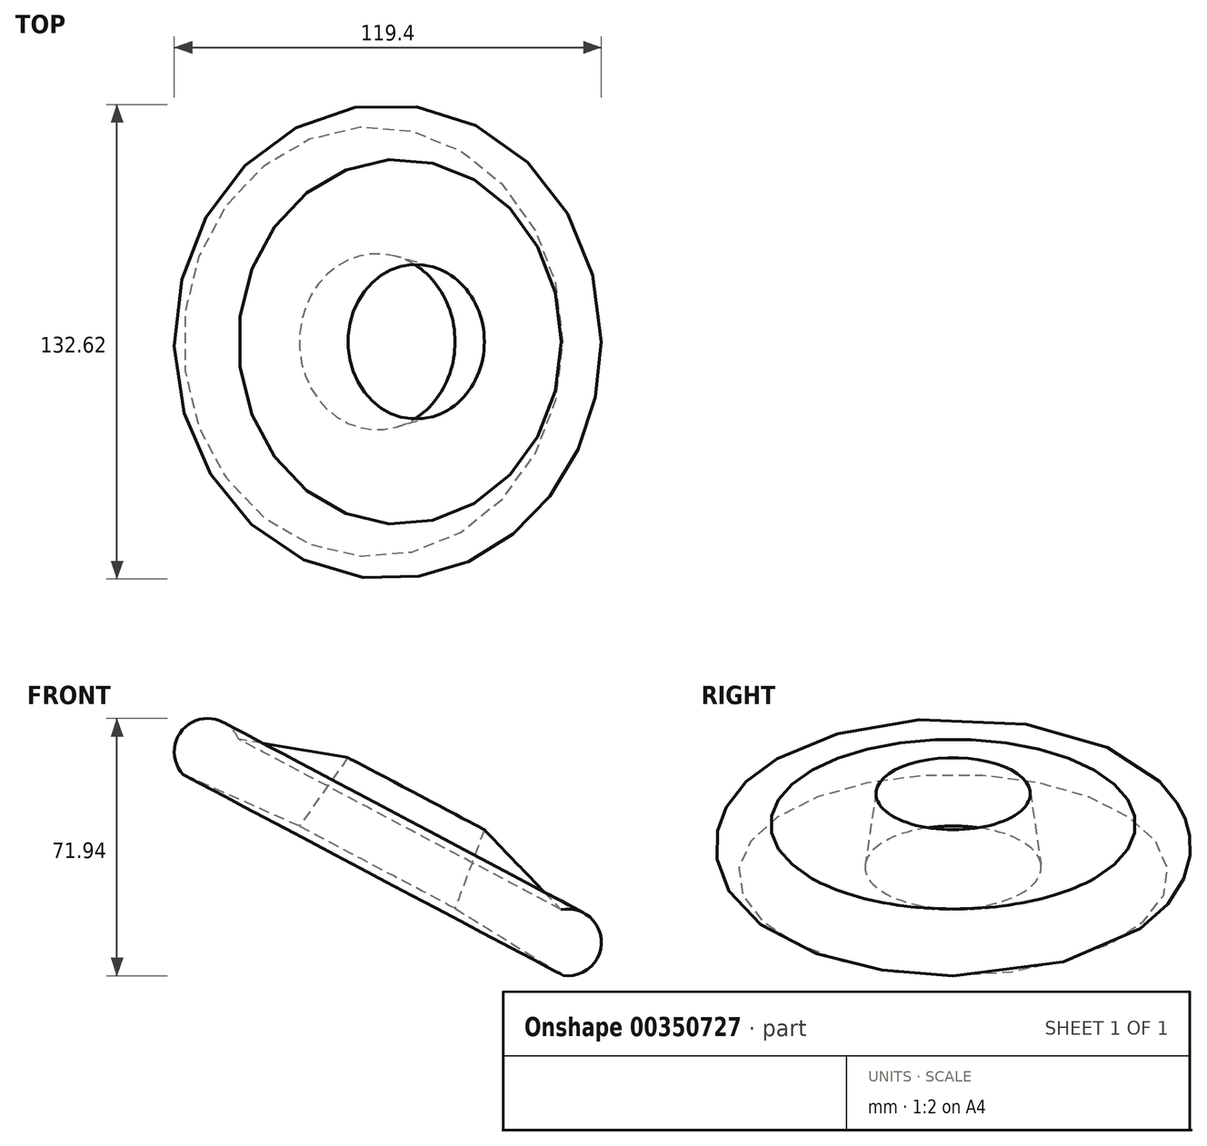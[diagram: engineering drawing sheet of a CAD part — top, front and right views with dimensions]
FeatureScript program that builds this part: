
annotation { "Feature Type Name" : "Feature", "Feature Type Description" : "" }
export const myFeature = defineFeature(function(context is Context, id is Id, definition is map)
    precondition{}
    {
        {
            var Q0;
            Q0=qCreatedBy(makeId("Front.planeOp"),FACE);
            var sketch = newSketch(context, id + "F0", { "sketchPlane" : qUnion([Q0])});
            skLineSegment(sketch, "E0", {"start": v(-60.22, 39.57) * mm, "end": v(-27.75, 25.16) * mm});
            skLineSegment(sketch, "E1", {"start": v(-27.75, 25.16) * mm, "end": v(-14.2, 44.3) * mm});
            skLineSegment(sketch, "E2", {"start": v(-14.2, 44.3) * mm, "end": v(-44.74, 49.47) * mm});
            skArc(sketch, "E3", {"start": v(-44.74, 49.47) * mm, "mid": v(-58.4, 53.79) * mm, "end": v(-60.22, 39.57) * mm});
            skLineSegment(sketch, "E4", {"start": v(12.52, 48.65) * mm, "end": v(-20.22, -13.25) * mm});
            skSolve(sketch);
        }
        {
            var Q0;
            Q0=makeQuery(id+"F0.imprint","IMPRINT",FACE,{"disambiguationData":[TD([[makeQuery(id+"F0.imprint","IMPRINT",EDGE,{"derivedFrom":sQuery(id+"F0.wireOp",EDGE,"E0")}),1.0]])]});
            var Q1;
            Q1=sQuery(id+"F0.wireOp",EDGE,"E0");
            var Q2;
            Q2=sQuery(id+"F0.wireOp",EDGE,"E3");
            var Q3;
            Q3=sQuery(id+"F0.wireOp",EDGE,"E2");
            var Q4;
            Q4=sQuery(id+"F0.wireOp",EDGE,"E1");
            var Q5;
            Q5=sQuery(id+"F0.wireOp",EDGE,"E4");
            revolve(context, id + "F1", {"surfaceOperationType" : NewSurfaceOperationType.NEW, "entities" : qUnion([Q0]), "surfaceEntities" : qUnion([Q1, Q2, Q3, Q4]), "axis" : qUnion([Q5]), "revolveType" : RevolveType.FULL});
        }
    });
